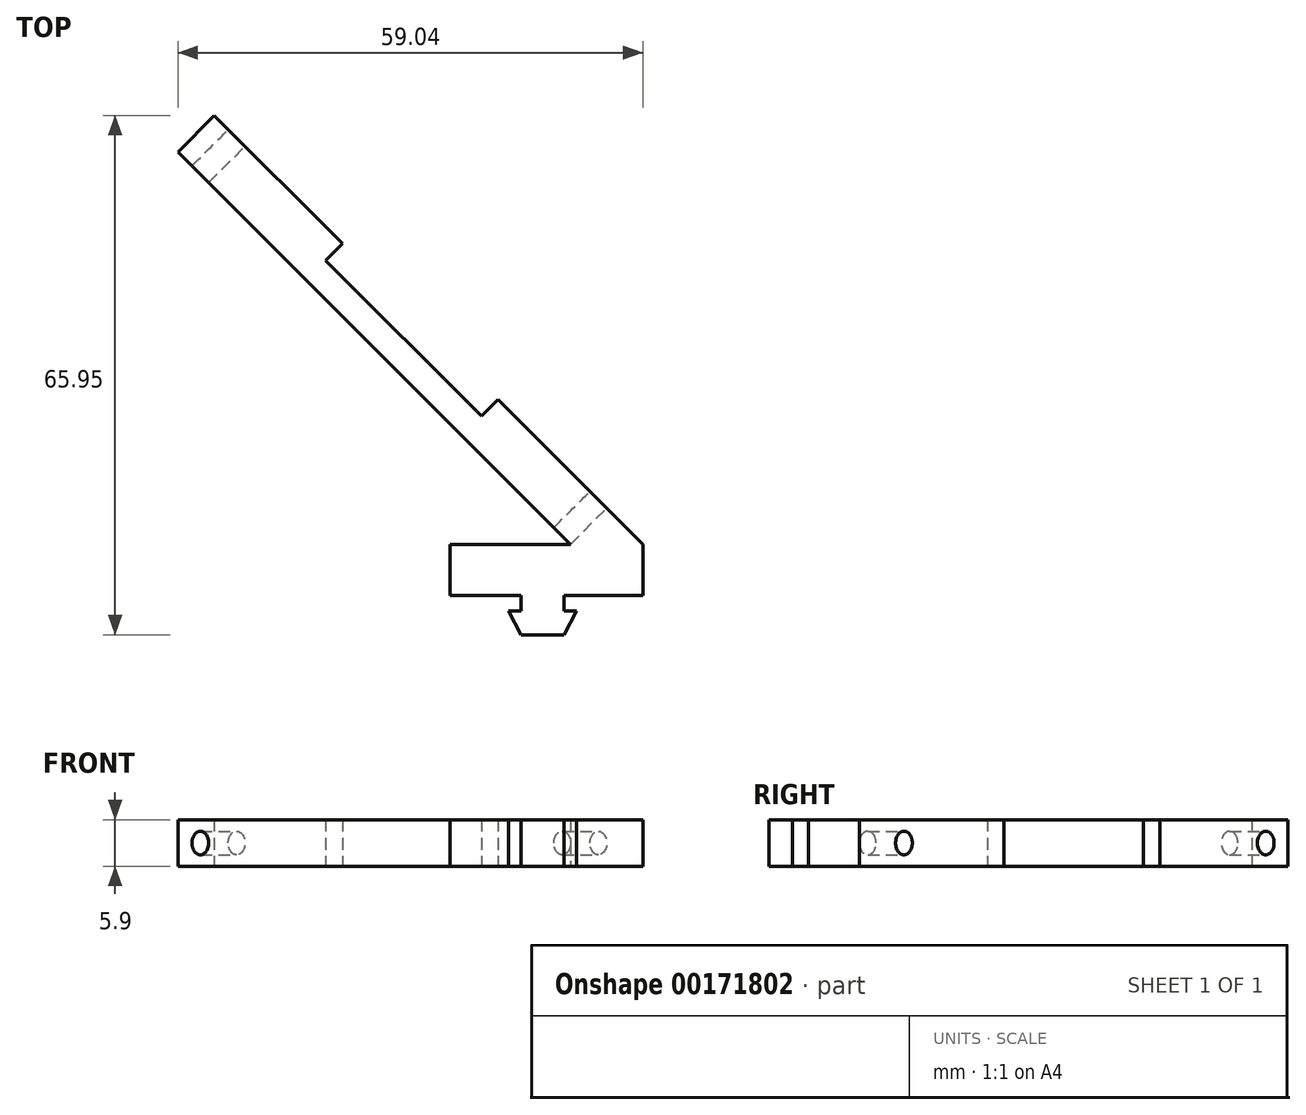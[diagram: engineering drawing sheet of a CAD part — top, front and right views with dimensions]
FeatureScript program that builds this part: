
annotation { "Feature Type Name" : "Feature", "Feature Type Description" : "" }
export const myFeature = defineFeature(function(context is Context, id is Id, definition is map)
    precondition{}
    {
        {
            var Q0;
            Q0=qCreatedBy(makeId("Top.planeOp"),FACE);
            var sketch = newSketch(context, id + "F0", { "sketchPlane" : qUnion([Q0])});
            skLineSegment(sketch, "E0.bottom", {"start": v(0, 0) * mm, "end": v(-10, 0) * mm});
            skLineSegment(sketch, "E0.top", {"start": v(-9.2, 6.5) * mm, "end": v(-24.5, 6.5) * mm});
            skLineSegment(sketch, "E0.left", {"start": v(0, 0) * mm, "end": v(0, 6.5) * mm});
            skLineSegment(sketch, "E0.right", {"start": v(-24.5, 0) * mm, "end": v(-24.5, 6.5) * mm});
            skLineSegment(sketch, "E1", {"start": v(0, 6.5) * mm, "end": v(-18.38, 24.88) * mm});
            skLineSegment(sketch, "E2", {"start": v(-54.45, 60.95) * mm, "end": v(-59.04, 56.35) * mm});
            skLineSegment(sketch, "E3", {"start": v(-59.04, 56.35) * mm, "end": v(-9.2, 6.5) * mm});
            skLineSegment(sketch, "E4", {"start": v(-15.5, 0) * mm, "end": v(-15.5, -2) * mm});
            skLineSegment(sketch, "E5", {"start": v(-15.5, -2) * mm, "end": v(-17.05, -2) * mm});
            skLineSegment(sketch, "E6", {"start": v(-17.05, -2) * mm, "end": v(-15.5, -5) * mm});
            skLineSegment(sketch, "E7", {"start": v(-15.5, -5) * mm, "end": v(-10, -5) * mm});
            skLineSegment(sketch, "E8", {"start": v(-10, -5) * mm, "end": v(-8.45, -2) * mm});
            skLineSegment(sketch, "E9", {"start": v(-8.45, -2) * mm, "end": v(-10, -2) * mm});
            skLineSegment(sketch, "E10", {"start": v(-10, -2) * mm, "end": v(-10, 0) * mm});
            skLineSegment(sketch, "E11.trimOffspring", {"start": v(-15.5, 0) * mm, "end": v(-24.5, 0) * mm});
            skLineSegment(sketch, "E12", {"start": v(-12.5, 5.32) * mm, "end": v(-2.58, 15.24) * mm, "construction": true});
            skLineSegment(sketch, "E13", {"start": v(-18.38, 24.88) * mm, "end": v(-20.5, 22.76) * mm});
            skLineSegment(sketch, "E14", {"start": v(-20.5, 22.76) * mm, "end": v(-40.3, 42.56) * mm});
            skLineSegment(sketch, "E15", {"start": v(-40.3, 42.56) * mm, "end": v(-38.18, 44.68) * mm});
            skLineSegment(sketch, "E16.trimOffspring", {"start": v(-38.18, 44.68) * mm, "end": v(-54.45, 60.95) * mm});
            skSolve(sketch);
        }
        {
            var Q0;
            Q0=makeQuery(id+"F0.imprint","IMPRINT",FACE,{"disambiguationData":[TD([[makeQuery(id+"F0.imprint","IMPRINT",EDGE,{"derivedFrom":sQuery(id+"F0.wireOp",EDGE,"E0.bottom")}),-1.0]])]});
            extrude(context, id + "F1", {"entities" : qUnion([Q0]), "depth" : 5.9 * mm});
        }
        {
            var Q0;
            Q0=makeQuery(id+"F1.opExtrude","SWEPT_FACE",FACE,{"disambiguationData":[OSD([sQuery(id+"F0.wireOp",EDGE,"E1")])]});
            var sketch = newSketch(context, id + "F2", { "sketchPlane" : qUnion([Q0])});
            skCircle(sketch, "E17", {"center": v(12.6, 2.95) * mm, "radius": 1.5 * mm});
            skPoint(sketch, "E17.centerSnap0", {"position": v(30.6, 2.95) * mm});
            skCircle(sketch, "E18", {"center": v(77.6, 2.95) * mm, "radius": 1.5 * mm});
            skSolve(sketch);
        }
        {
            var Q0;
            Q0=makeQuery(id+"F2.imprint","IMPRINT",FACE,{"disambiguationData":[TD([[makeQuery(id+"F2.imprint","IMPRINT",EDGE,{"derivedFrom":sQuery(id+"F2.wireOp",EDGE,"E18")}),1.0]])]});
            var Q1;
            Q1=makeQuery(id+"F2.imprint","IMPRINT",FACE,{"disambiguationData":[TD([[makeQuery(id+"F2.imprint","IMPRINT",EDGE,{"derivedFrom":sQuery(id+"F2.wireOp",EDGE,"E17")}),1.0]])]});
            extrude(context, id + "F3", {"entities" : qUnion([Q0, Q1]), "operationType" : NewBodyOperationType.REMOVE, "endBound" : BoundingType.UP_TO_NEXT, "oppositeDirection" : true, "depth" : 25 * mm});
        }
    });
